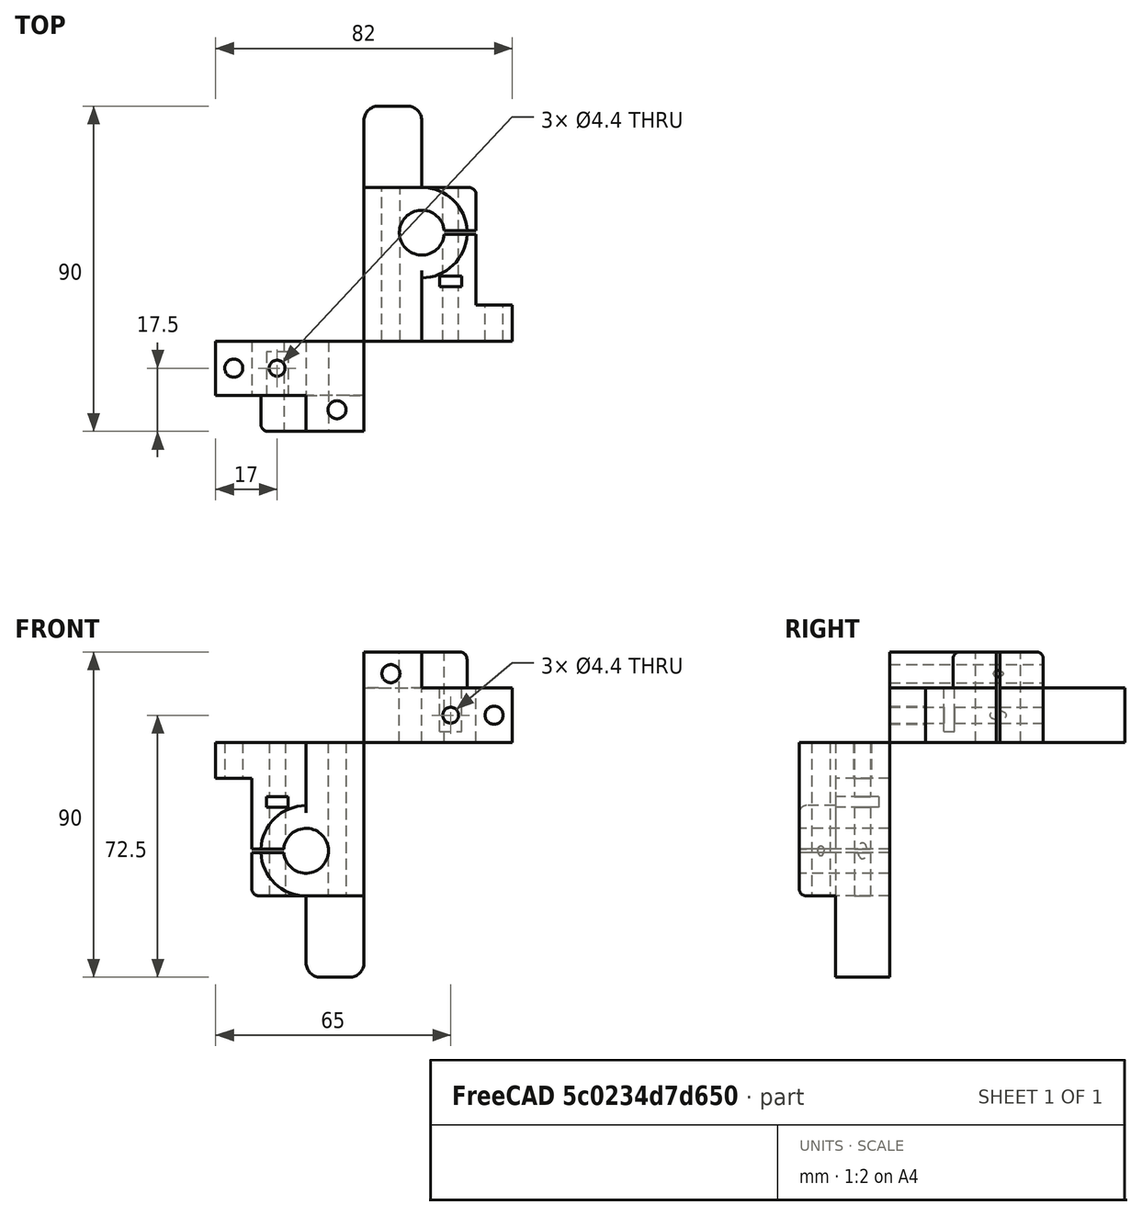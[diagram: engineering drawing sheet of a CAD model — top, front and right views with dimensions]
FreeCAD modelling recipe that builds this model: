
FCSTD DOCUMENT  (FreeCAD 0.15R4664 (Git))
Label: foot_R
License: All rights reserved
LicenseURL: http://en.wikipedia.org/wiki/All_rights_reserved
objects: Part::Box×6, Part::Cut×6, Part::Cylinder×5, Part::Feature×3, Part::MultiFuse×3, Part::Fillet×3, Mesh::Feature×1
note: 26 computed .brp shape members not serialized (recipe doc carries the construction recipe); baked Part::Feature solids carry a one-line shape summary decoded from their .brp

FEATURE [Mesh::Feature] footR_12mm
FEATURE [Part::Feature] footR_12mm001001  label="footR_12mm002"
  shape: bbox 41 x 65 x 25 mm, 3425 faces, 0 solids (baked)
FEATURE [Part::Box] Box  label="Cubo"
  Height = 15
  Length = 41
  Width = 65
FEATURE [Part::Box] Box001  label="Cubo001"
  Height = 10
  Length = 16
  Placement = pos=(0,0,15) rot=(0,0,1;0rad)
  Width = 42.5
FEATURE [Part::Cylinder] Cylinder  label="Cilindro"
  Angle = 360
  Height = 10
  Placement = pos=(16,30,15) rot=(0,0,1;3.14159rad)
  Radius = 12.5
FEATURE [Part::Box] Box002  label="Cubo002"
  Height = 15
  Length = 10
  Placement = pos=(31,10,0) rot=(0,0,1;0rad)
  Width = 55
FEATURE [Part::Box] Box003  label="Cubo003"
  Height = 15
  Length = 15
  Placement = pos=(16,42.5,0) rot=(0,0,1;0rad)
  Width = 22.5
FEATURE [Part::Box] Box004  label="Cubo004"
  Height = 27
  Length = 20
  Placement = pos=(14,29.5,-1) rot=(0,0,1;0rad)
  Width = 1
FEATURE [Part::Box] Box005  label="Cubo005"
  Height = 17
  Length = 6
  Placement = pos=(21,15,3) rot=(0,0,1;0rad)
  Width = 3
FEATURE [Part::Cylinder] Cylinder001  label="Cilindro001"
  Angle = 360
  Height = 30
  Placement = pos=(16,30,-2) rot=(0,0,1;0rad)
  Radius = 6.2
FEATURE [Part::Cylinder] Cylinder002  label="Cilindro002"
  Angle = 360
  Height = 45
  Placement = pos=(7.45,-1,19) rot=(-1,0,0;1.5708rad)
  Radius = 2.5
FEATURE [Part::Cylinder] Cylinder003  label="Cilindro003"
  Angle = 360
  Height = 45
  Placement = pos=(24,-1,7.5) rot=(-1,0,0;1.5708rad)
  Radius = 2.2
FEATURE [Part::Cylinder] Cylinder004  label="Cilindro004"
  Angle = 360
  Height = 12
  Placement = pos=(36,-1,7.5) rot=(-1,0,0;1.5708rad)
  Radius = 2.5
FEATURE [Part::Cut] Cut
  Base = -> Box
  Tool = -> Box002
FEATURE [Part::Cut] Cut001
  Base = -> Cut
  Tool = -> Box003
FEATURE [Part::MultiFuse] Fusion
  Shapes = -> [Box001,Cut001]
FEATURE [Part::MultiFuse] Fusion001
  Shapes = -> [Fusion,Cylinder]
FEATURE [Part::Cut] Cut002
  Base = -> Fusion001
  Tool = -> Cylinder001
FEATURE [Part::Cut] Cut003
  Base = -> Cut002
  Tool = -> Box004
FEATURE [Part::Cut] Cut004
  Base = -> Cut003
  Tool = -> Box005
FEATURE [Part::MultiFuse] Fusion002
  Shapes = -> [Cylinder002,Cylinder003,Cylinder004]
FEATURE [Part::Cut] Cut005
  Base = -> Cut004
  Tool = -> Fusion002
FEATURE [Part::Fillet] Fillet
  Base = -> Cut005
  Edges = 2 edges r=2: [Edge66,Edge68]
FEATURE [Part::Fillet] Fillet001
  Base = -> Fillet
  Edges = 1 edges r=2: [Edge26]
FEATURE [Part::Fillet] Fillet002
  Base = -> Fillet001
  Edges = 2 edges r=4: [Edge34,Edge59]
FEATURE [Part::Feature] Fillet002_solid  label="Fillet002 (Solid)"
  shape: bbox 41.01 x 65.01 x 25.01 mm, 37 faces (baked)
FEATURE [Part::Feature] Fillet002_solid001  label="Fillet002 (Solid)001"
  Placement = pos=(0,0,0) rot=(0,-0.707107,0.707107;3.14159rad)
  shape: bbox 41.01 x 25.01 x 65.01 mm, 37 faces (baked)
